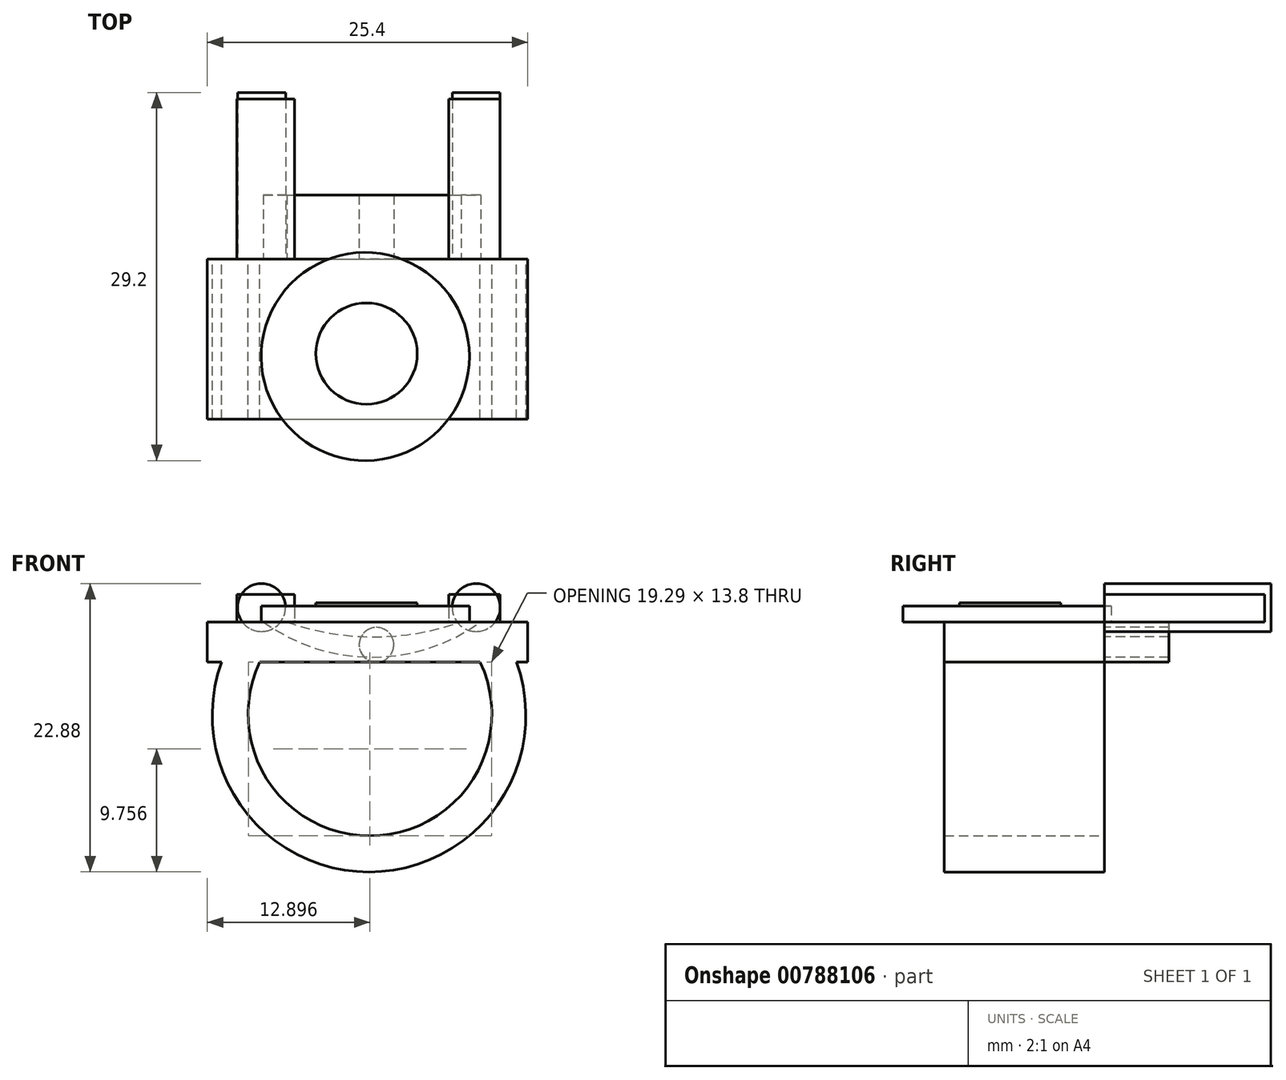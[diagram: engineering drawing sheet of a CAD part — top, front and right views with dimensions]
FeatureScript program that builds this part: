
annotation { "Feature Type Name" : "Feature", "Feature Type Description" : "" }
export const myFeature = defineFeature(function(context is Context, id is Id, definition is map)
    precondition{}
    {
        {
            var Q0;
            Q0=qCreatedBy(makeId("Top.planeOp"),FACE);
            var sketch = newSketch(context, id + "F0", { "sketchPlane" : qUnion([Q0])});
            skLineSegment(sketch, "E0.bottom", {"start": v(-13.4, 0) * mm, "end": v(12, 0) * mm});
            skLineSegment(sketch, "E0.top", {"start": v(-13.4, -12.7) * mm, "end": v(12, -12.7) * mm});
            skLineSegment(sketch, "E0.left", {"start": v(-13.4, 0) * mm, "end": v(-13.4, -12.7) * mm});
            skLineSegment(sketch, "E0.right", {"start": v(12, 0) * mm, "end": v(12, -12.7) * mm});
            skSolve(sketch);
        }
        {
            var Q0;
            Q0 = qSketchRegion(id + "F0", true);
            extrude(context, id + "F1", {"entities" : qUnion([Q0]), "oppositeDirection" : true, "depth" : 3.17 * mm, "offsetDistance" : 25.4 * mm});
        }
        {
            var Q0;
            Q0=qCreatedBy(makeId("Front.planeOp"),FACE);
            var sketch = newSketch(context, id + "F2", { "sketchPlane" : qUnion([Q0])});
            skArc(sketch, "E1", {"start": v(-10.57, 0) * mm, "mid": v(-0.59, -19.83) * mm, "end": v(9.4, 0) * mm});
            skArc(sketch, "E2", {"start": v(-6.83, 0) * mm, "mid": v(-0.51, -16.97) * mm, "end": v(5.8, 0) * mm});
            skLineSegment(sketch, "E3", {"start": v(-10.57, 0) * mm, "end": v(-6.83, 0) * mm});
            skLineSegment(sketch, "E4", {"start": v(5.8, 0) * mm, "end": v(9.4, 0) * mm});
            skSolve(sketch);
        }
        {
            var Q0;
            Q0 = qSketchRegion(id + "F2", true);
            extrude(context, id + "F3", {"entities" : qUnion([Q0]), "operationType" : NewBodyOperationType.ADD, "depth" : 12.7 * mm, "offsetDistance" : 25.4 * mm});
        }
        {
            var Q0;
            Q0=qCreatedBy(makeId("Top.planeOp"),FACE);
            var sketch = newSketch(context, id + "F4", { "sketchPlane" : qUnion([Q0])});
            skCircle(sketch, "E5", {"center": v(-0.88, -7.73) * mm, "radius": 8.26 * mm});
            skSolve(sketch);
        }
        {
            var Q0;
            Q0 = qSketchRegion(id + "F4", true);
            extrude(context, id + "F5", {"entities" : qUnion([Q0]), "operationType" : NewBodyOperationType.ADD, "depth" : 1.27 * mm, "offsetDistance" : 25.4 * mm});
        }
        {
            var Q0;
            Q0=qCreatedBy(makeId("Top.planeOp"),FACE);
            var sketch = newSketch(context, id + "F6", { "sketchPlane" : qUnion([Q0])});
            skCircle(sketch, "E6", {"center": v(-0.79, -7.5) * mm, "radius": 4.02 * mm});
            skSolve(sketch);
        }
        {
            var Q0;
            Q0 = qSketchRegion(id + "F6", true);
            extrude(context, id + "F7", {"entities" : qUnion([Q0]), "operationType" : NewBodyOperationType.ADD, "depth" : 1.52 * mm, "offsetDistance" : 25.4 * mm});
        }
        {
            var Q0;
            Q0=qCreatedBy(makeId("Front.planeOp"),FACE);
            var sketch = newSketch(context, id + "F8", { "sketchPlane" : qUnion([Q0])});
            skLineSegment(sketch, "E7.bottom", {"start": v(9.8, 2.18) * mm, "end": v(5.73, 2.18) * mm});
            skLineSegment(sketch, "E7.top", {"start": v(9.8, 0) * mm, "end": v(5.73, 0) * mm});
            skLineSegment(sketch, "E7.left", {"start": v(9.8, 2.18) * mm, "end": v(9.8, 0) * mm});
            skLineSegment(sketch, "E7.right", {"start": v(5.73, 2.18) * mm, "end": v(5.73, 0) * mm});
            skLineSegment(sketch, "E8.bottom", {"start": v(-6.49, 2.18) * mm, "end": v(-11.06, 2.18) * mm});
            skLineSegment(sketch, "E8.top", {"start": v(-6.49, 0) * mm, "end": v(-11.06, 0) * mm});
            skLineSegment(sketch, "E8.left", {"start": v(-6.49, 2.18) * mm, "end": v(-6.49, 0) * mm});
            skLineSegment(sketch, "E8.right", {"start": v(-11.06, 2.18) * mm, "end": v(-11.06, 0) * mm});
            skSolve(sketch);
        }
        {
            var Q0;
            Q0 = qSketchRegion(id + "F8", true);
            extrude(context, id + "F9", {"entities" : qUnion([Q0]), "oppositeDirection" : true, "depth" : 12.7 * mm, "offsetDistance" : 25.4 * mm});
        }
        {
            var Q0;
            Q0=qCreatedBy(makeId("Front.planeOp"),FACE);
            var sketch = newSketch(context, id + "F10", { "sketchPlane" : qUnion([Q0])});
            skArc(sketch, "E9", {"start": v(-8.97, 0) * mm, "mid": v(-0.35, -2.8) * mm, "end": v(8.26, 0) * mm});
            skArc(sketch, "E10", {"start": v(-7.1, 0) * mm, "mid": v(-0.2, -1.18) * mm, "end": v(6.7, 0) * mm});
            skLineSegment(sketch, "E11", {"start": v(8.26, 0) * mm, "end": v(6.7, 0) * mm});
            skLineSegment(sketch, "E12", {"start": v(-7.1, 0) * mm, "end": v(-8.97, 0) * mm});
            skSolve(sketch);
        }
        {
            var Q0;
            Q0 = qSketchRegion(id + "F10", true);
            extrude(context, id + "F11", {"entities" : qUnion([Q0]), "oppositeDirection" : true, "depth" : 5.08 * mm, "offsetDistance" : 25.4 * mm});
        }
        {
            var Q0;
            Q0=qCreatedBy(makeId("Front.planeOp"),FACE);
            var sketch = newSketch(context, id + "F12", { "sketchPlane" : qUnion([Q0])});
            skCircle(sketch, "E13", {"center": v(-9.11, 1.15) * mm, "radius": 1.9 * mm});
            skCircle(sketch, "E14", {"center": v(7.9, 1.15) * mm, "radius": 1.9 * mm});
            skSolve(sketch);
        }
        {
            var Q0;
            Q0 = qSketchRegion(id + "F12", true);
            extrude(context, id + "F13", {"entities" : qUnion([Q0]), "oppositeDirection" : true, "depth" : 13.2 * mm, "offsetDistance" : 25.4 * mm});
        }
        {
            var Q0;
            Q0=qCreatedBy(makeId("Front.planeOp"),FACE);
            var sketch = newSketch(context, id + "F14", { "sketchPlane" : qUnion([Q0])});
            skCircle(sketch, "E15", {"center": v(0, -1.8) * mm, "radius": 1.37 * mm});
            skSolve(sketch);
        }
        {
            var Q0;
            Q0 = qSketchRegion(id + "F14", true);
            extrude(context, id + "F15", {"entities" : qUnion([Q0]), "oppositeDirection" : true, "depth" : 5.08 * mm, "offsetDistance" : 25.4 * mm});
        }
    });
